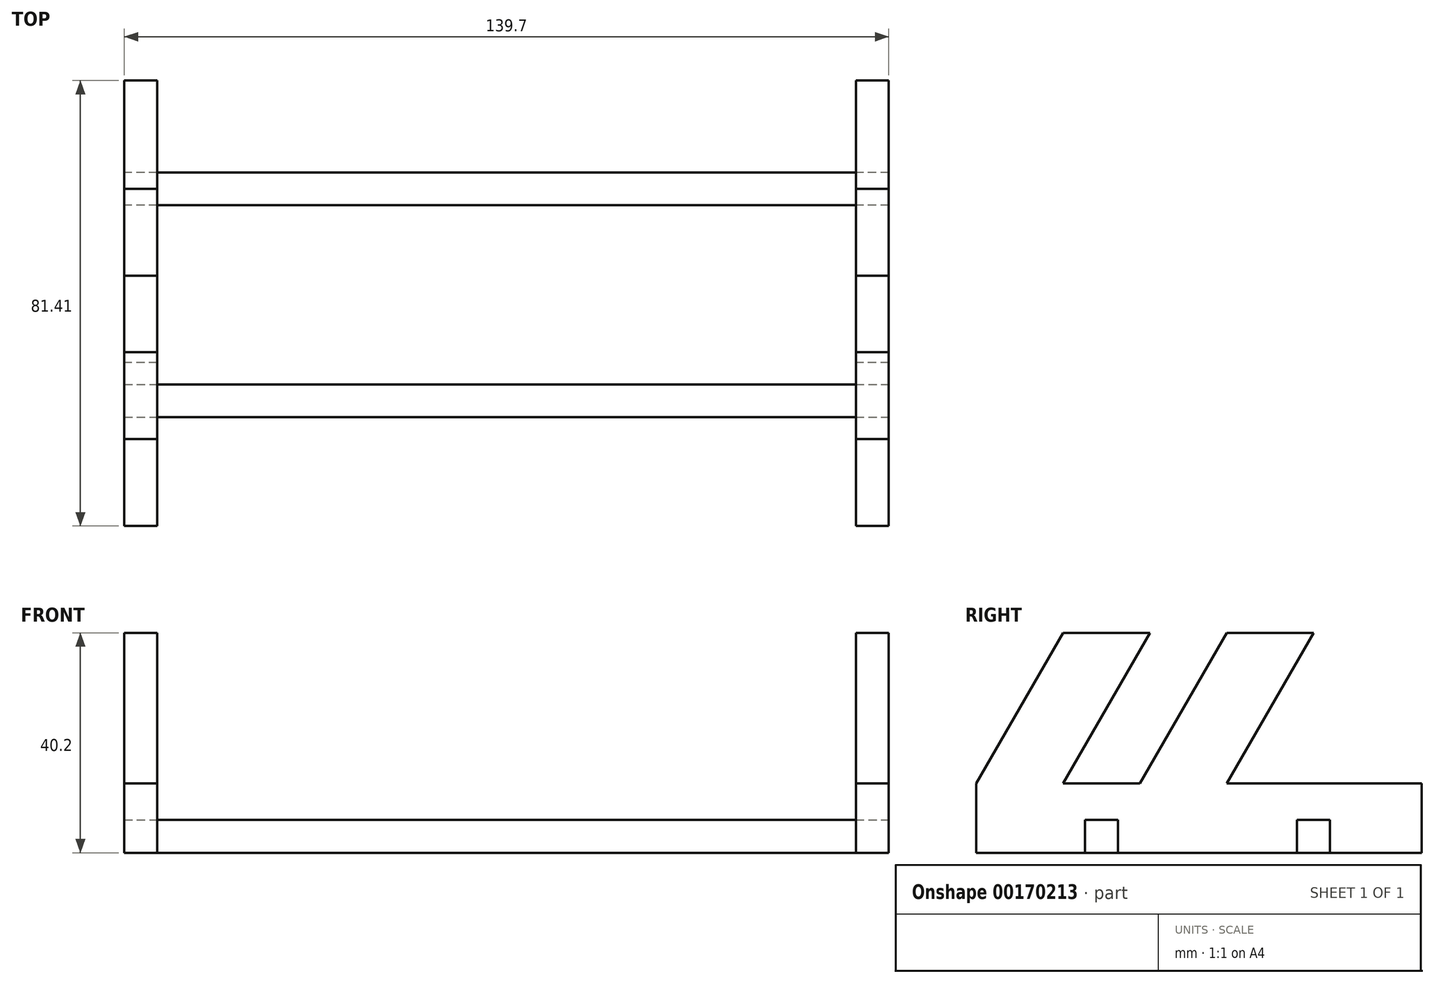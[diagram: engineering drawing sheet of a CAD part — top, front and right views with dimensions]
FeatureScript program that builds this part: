
annotation { "Feature Type Name" : "Feature", "Feature Type Description" : "" }
export const myFeature = defineFeature(function(context is Context, id is Id, definition is map)
    precondition{}
    {
        {
            var Q0;
            Q0=qCreatedBy(makeId("Right.planeOp"),FACE);
            var sketch = newSketch(context, id + "F0", { "sketchPlane" : qUnion([Q0])});
            skLineSegment(sketch, "E0", {"start": v(20.69, -31.19) * mm, "end": v(20.69, -18.49) * mm});
            skLineSegment(sketch, "E1", {"start": v(-14.97, -18.49) * mm, "end": v(0.9, 9) * mm});
            skLineSegment(sketch, "E2", {"start": v(0.9, 9) * mm, "end": v(-14.97, 9) * mm});
            skLineSegment(sketch, "E3", {"start": v(-14.97, 9) * mm, "end": v(-30.84, -18.49) * mm});
            skLineSegment(sketch, "E4", {"start": v(-30.84, -18.49) * mm, "end": v(-44.84, -18.49) * mm});
            skLineSegment(sketch, "E5", {"start": v(-44.84, -18.49) * mm, "end": v(-28.97, 9) * mm});
            skLineSegment(sketch, "E6", {"start": v(-44.84, 9) * mm, "end": v(-28.97, 9) * mm});
            skLineSegment(sketch, "E7", {"start": v(-30.84, -18.49) * mm, "end": v(-14.97, -18.49) * mm, "construction": true});
            skLineSegment(sketch, "E8", {"start": v(-28.97, 9) * mm, "end": v(-14.97, 9) * mm, "construction": true});
            skLineSegment(sketch, "E9", {"start": v(-60.72, -18.49) * mm, "end": v(-60.72, -31.19) * mm});
            skLineSegment(sketch, "E10", {"start": v(-44.84, 9) * mm, "end": v(-60.72, -18.49) * mm});
            skLineSegment(sketch, "E11", {"start": v(-14.97, -18.49) * mm, "end": v(0.9, -18.49) * mm});
            skLineSegment(sketch, "E12", {"start": v(20.69, -18.49) * mm, "end": v(0.9, -18.49) * mm});
            skLineSegment(sketch, "E13", {"start": v(0.9, 9) * mm, "end": v(0.9, -18.49) * mm, "construction": true});
            skLineSegment(sketch, "E14", {"start": v(-40.84, -31.19) * mm, "end": v(-40.84, -25.19) * mm});
            skLineSegment(sketch, "E15", {"start": v(-40.84, -25.19) * mm, "end": v(-34.84, -25.19) * mm});
            skLineSegment(sketch, "E16", {"start": v(-34.84, -25.19) * mm, "end": v(-34.84, -31.19) * mm});
            skLineSegment(sketch, "E17", {"start": v(-40.84, -31.19) * mm, "end": v(-60.72, -31.19) * mm});
            skLineSegment(sketch, "E18", {"start": v(-37.84, -18.49) * mm, "end": v(-37.84, -25.19) * mm, "construction": true});
            skLineSegment(sketch, "E19", {"start": v(-40.84, -31.19) * mm, "end": v(-34.84, -31.19) * mm, "construction": true});
            skLineSegment(sketch, "E20", {"start": v(-2.1, -31.19) * mm, "end": v(-2.1, -25.19) * mm});
            skLineSegment(sketch, "E21", {"start": v(-2.1, -25.19) * mm, "end": v(3.9, -25.19) * mm});
            skLineSegment(sketch, "E22", {"start": v(3.9, -25.19) * mm, "end": v(3.9, -31.19) * mm});
            skLineSegment(sketch, "E23", {"start": v(3.9, -31.19) * mm, "end": v(20.69, -31.19) * mm});
            skLineSegment(sketch, "E24", {"start": v(-2.1, -31.19) * mm, "end": v(-34.84, -31.19) * mm});
            skLineSegment(sketch, "E25", {"start": v(0.9, -18.49) * mm, "end": v(0.9, -25.19) * mm, "construction": true});
            skSolve(sketch);
        }
        {
            var Q0;
            Q0 = qSketchRegion(id + "F0", true);
            extrude(context, id + "F1", {"entities" : qUnion([Q0]), "depth" : 6 * mm});
        }
        {
            var Q0;
            Q0=makeQuery(id+"F1.opExtrude","SWEPT_BODY",BODY,{"disambiguationData":[OSD([sQuery(id+"F0.wireOp",EDGE,"E0"),sQuery(id+"F0.wireOp",EDGE,"E1"),sQuery(id+"F0.wireOp",EDGE,"E2"),sQuery(id+"F0.wireOp",EDGE,"E3"),sQuery(id+"F0.wireOp",EDGE,"E4"),sQuery(id+"F0.wireOp",EDGE,"E5"),sQuery(id+"F0.wireOp",EDGE,"E6"),sQuery(id+"F0.wireOp",EDGE,"E9"),sQuery(id+"F0.wireOp",EDGE,"E10"),sQuery(id+"F0.wireOp",EDGE,"E11"),sQuery(id+"F0.wireOp",EDGE,"E12"),sQuery(id+"F0.wireOp",EDGE,"E14"),sQuery(id+"F0.wireOp",EDGE,"E15"),sQuery(id+"F0.wireOp",EDGE,"E16"),sQuery(id+"F0.wireOp",EDGE,"E17"),sQuery(id+"F0.wireOp",EDGE,"E20"),sQuery(id+"F0.wireOp",EDGE,"E21"),sQuery(id+"F0.wireOp",EDGE,"E22"),sQuery(id+"F0.wireOp",EDGE,"E23"),sQuery(id+"F0.wireOp",EDGE,"E24")])]});
            transform(context, id + "F2", {"entities" : qUnion([Q0]), "transformType" : TransformType.TRANSLATION_3D, "dx" : 139.7 * mm - 6 * mm, "dy" : 0 * mm, "dz" : 0 * mm, "makeCopy" : true});
        }
        {
            var Q0;
            Q0=makeQuery(id+"F2.opPattern","COPY",FACE,{"derivedFrom":makeQuery(id+"F1.opExtrude","CAP_FACE",FACE,{"disambiguationData":[OSD([sQuery(id+"F0.wireOp",EDGE,"E0"),sQuery(id+"F0.wireOp",EDGE,"E1"),sQuery(id+"F0.wireOp",EDGE,"E2"),sQuery(id+"F0.wireOp",EDGE,"E3"),sQuery(id+"F0.wireOp",EDGE,"E4"),sQuery(id+"F0.wireOp",EDGE,"E5"),sQuery(id+"F0.wireOp",EDGE,"E6"),sQuery(id+"F0.wireOp",EDGE,"E9"),sQuery(id+"F0.wireOp",EDGE,"E10"),sQuery(id+"F0.wireOp",EDGE,"E11"),sQuery(id+"F0.wireOp",EDGE,"E12"),sQuery(id+"F0.wireOp",EDGE,"E14"),sQuery(id+"F0.wireOp",EDGE,"E15"),sQuery(id+"F0.wireOp",EDGE,"E16"),sQuery(id+"F0.wireOp",EDGE,"E17"),sQuery(id+"F0.wireOp",EDGE,"E20"),sQuery(id+"F0.wireOp",EDGE,"E21"),sQuery(id+"F0.wireOp",EDGE,"E22"),sQuery(id+"F0.wireOp",EDGE,"E23"),sQuery(id+"F0.wireOp",EDGE,"E24")])],"isStart":false}),"instanceName":"1"});
            var sketch = newSketch(context, id + "F3", { "sketchPlane" : qUnion([Q0])});
            skLineSegment(sketch, "E26.bottom", {"start": v(-40.84, -25.19) * mm, "end": v(-34.84, -25.19) * mm});
            skLineSegment(sketch, "E26.top", {"start": v(-40.84, -31.19) * mm, "end": v(-34.84, -31.19) * mm});
            skLineSegment(sketch, "E26.left", {"start": v(-40.84, -25.19) * mm, "end": v(-40.84, -31.19) * mm});
            skLineSegment(sketch, "E26.right", {"start": v(-34.84, -25.19) * mm, "end": v(-34.84, -31.19) * mm});
            skLineSegment(sketch, "E27.bottom", {"start": v(-2.1, -25.19) * mm, "end": v(3.9, -25.19) * mm});
            skLineSegment(sketch, "E27.top", {"start": v(-2.1, -31.19) * mm, "end": v(3.9, -31.19) * mm});
            skLineSegment(sketch, "E27.left", {"start": v(-2.1, -25.19) * mm, "end": v(-2.1, -31.19) * mm});
            skLineSegment(sketch, "E27.right", {"start": v(3.9, -25.19) * mm, "end": v(3.9, -31.19) * mm});
            skSolve(sketch);
        }
        {
            var Q0;
            Q0 = qSketchRegion(id + "F3", true);
            extrude(context, id + "F4", {"entities" : qUnion([Q0]), "oppositeDirection" : true, "depth" : 139.7 * mm});
        }
    });
